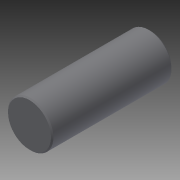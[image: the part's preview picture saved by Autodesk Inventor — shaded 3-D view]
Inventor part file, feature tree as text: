
AUTODESK INVENTOR PART (.ipt)
format: ipt  version: 2014 (Build 180170000, 170)  size: 103,936 bytes
history: native  units: in
note: dims shown in document units (in); Inventor stores cm internally (conversion verified against a paired STEP export)
features: other x35, revolve x1, sketch x1
ambient origin geometry x8: Origin, YZ Plane, XZ Plane, XY Plane, X Axis, Y Axis, Z Axis, Center Point
bodies: Solid1 (feature_tree)
feature tree (37):
  revolve  "Revolution1"  [1 undecoded]
  other  "dia1_XY"
  other  "dia1_YZ"
  other  "dia1_ZX"
  other  "dia1_X"
  other  "dia1_Y"
  other  "dia1_Z"
  other  "dia1_Center"
  other  "dia2_XY"
  other  "dia2_YZ"
  other  "dia2_ZX"
  other  "dia2_X"
  other  "dia2_Y"
  other  "dia2_Z"
  other  "dia2_Center"
  other  "pin_XY"
  other  "pin_YZ"
  other  "pin_ZX"
  other  "pin_X"
  other  "pin_Y"
  other  "pin_Z"
  other  "pin_Center"
  other  "pin1_XY"
  other  "pin1_YZ"
  other  "pin1_ZX"
  other  "pin1_X"
  other  "pin1_Y"
  other  "pin1_Z"
  other  "pin1_Center"
  other  "pin2_XY"
  other  "pin2_YZ"
  other  "pin2_ZX"
  other  "pin2_X"
  other  "pin2_Y"
  other  "pin2_Z"
  other  "pin2_Center"
  sketch  "Sketch_1"  dims[d0=360.0deg]
note: 1 required parameter value undecoded (feature->parameter linkage not recoverable at this tier; creation-order binding heuristic only, values carry confidence <= 0.55)
